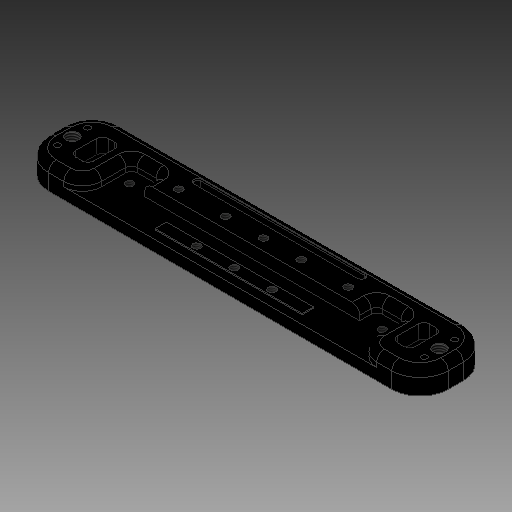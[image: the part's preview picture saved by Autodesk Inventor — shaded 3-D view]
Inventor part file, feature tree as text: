
AUTODESK INVENTOR PART (.ipt)
format: ipt  version: 2019 (Build 230136000, 136)  size: 331,776 bytes
history: native  units: mm
features: other x9, extrude x4, hole x4, fillet x1, chamfer x1
ambient origin geometry x8: Origin, YZ Plane, XZ Plane, XY Plane, X Axis, Y Axis, Z Axis, Center Point
bodies: Solid1 (feature_tree), Body (feature_tree)
feature tree (19):
  extrude  "Metal Band Cutout"  Depth=212.0mm
  extrude  "Metal Band Clamp"  Depth=106.0mm
  extrude  "Lower Skin Passage"  Depth=38.0mm
  extrude  "Rail Cutouts"  Depth=19.0mm
  hole  "Dowel Pin Holes"  [1 undecoded]
  hole  "Fastening Holes"  [1 undecoded]
  hole  "Clamp Holes"  [1 undecoded]
  hole  "Rail Holes"  [1 undecoded]
  fillet  "Body Fillet"  Radius=114.0mm
  chamfer  "Lower Skin Passage Chamfer"  Distance=17.0mm
  other  "Body Outline"
  other  "Metal Band Cutout Outline"
  other  "Metal Band Clamp Outline"
  other  "Lower Skin Passage Outline"
  other  "Rail Cutouts Outline"
  other  "Dowel Pin Hole Positions"
  other  "Clamp Hole Positions"
  other  "Rail Hole Positions"
  other  "Fastening Hole Positions"
note: 4 required parameter values undecoded (feature->parameter linkage not recoverable at this tier; creation-order binding heuristic only, values carry confidence <= 0.55)
